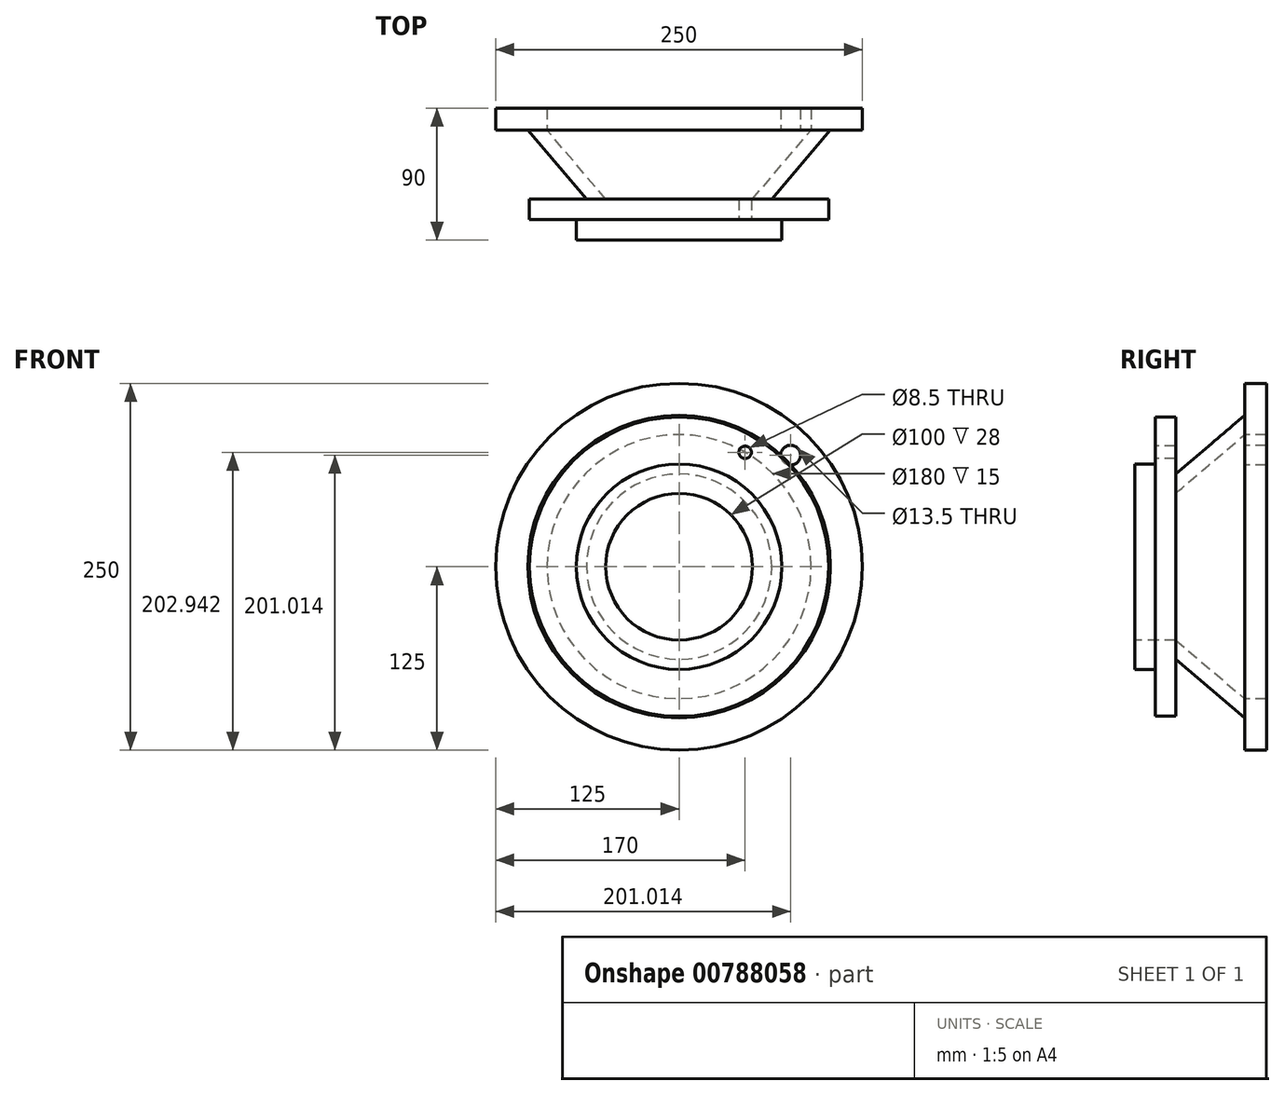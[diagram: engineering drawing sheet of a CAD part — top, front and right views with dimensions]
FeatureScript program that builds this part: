
annotation { "Feature Type Name" : "Feature", "Feature Type Description" : "" }
export const myFeature = defineFeature(function(context is Context, id is Id, definition is map)
    precondition{}
    {
        {
            var Q0;
            Q0=qCreatedBy(makeId("Front.planeOp"),FACE);
            var sketch = newSketch(context, id + "F0", { "sketchPlane" : qUnion([Q0])});
            skCircle(sketch, "E0", {"center": v(0, 0) * mm, "radius": 125 * mm});
            skSolve(sketch);
        }
        {
            var Q0;
            Q0=makeQuery(id+"F0.imprint","IMPRINT",FACE,{"disambiguationData":[TD([[makeQuery(id+"F0.imprint","IMPRINT",EDGE,{"derivedFrom":sQuery(id+"F0.wireOp",EDGE,"E0")}),1.0]])]});
            extrude(context, id + "F1", {"entities" : qUnion([Q0]), "depth" : 15 * mm, "offsetDistance" : 25 * mm});
        }
        {
            var Q0;
            Q0=makeQuery(id+"F1.opExtrude","CAP_FACE",FACE,{"disambiguationData":[OSD([sQuery(id+"F0.wireOp",EDGE,"E0")])],"isStart":false});
            var sketch = newSketch(context, id + "F2", { "sketchPlane" : qUnion([Q0])});
            skCircle(sketch, "E1", {"center": v(0, 0) * mm, "radius": 90 * mm});
            skSolve(sketch);
        }
        {
            var Q0;
            Q0=makeQuery(id+"F2.imprint","IMPRINT",FACE,{"disambiguationData":[TD([[makeQuery(id+"F2.imprint","IMPRINT",EDGE,{"derivedFrom":sQuery(id+"F2.wireOp",EDGE,"E1")}),-1.0]])]});
            cPlane(context, id + "F3", {"entities" : qUnion([Q0]), "cplaneType" : CPlaneType.OFFSET, "offset" : 47 * mm, "width" : 150 * mm, "height" : 150 * mm});
        }
        {
            var Q0;
            Q0=qCreatedBy(id+"F3.planeOp",FACE);
            var sketch = newSketch(context, id + "F4", { "sketchPlane" : qUnion([Q0])});
            skCircle(sketch, "E2", {"center": v(0, 0) * mm, "radius": 102 * mm});
            skSolve(sketch);
        }
        {
            var Q0;
            Q0=makeQuery(id+"F4.imprint","IMPRINT",FACE,{"disambiguationData":[TD([[makeQuery(id+"F4.imprint","IMPRINT",EDGE,{"derivedFrom":sQuery(id+"F4.wireOp",EDGE,"E2")}),1.0]])]});
            extrude(context, id + "F5", {"entities" : qUnion([Q0]), "depth" : 14 * mm, "offsetDistance" : 25 * mm});
        }
        {
            var Q0;
            Q0=makeQuery(id+"F5.opExtrude","CAP_FACE",FACE,{"disambiguationData":[OSD([sQuery(id+"F4.wireOp",EDGE,"E2")])],"isStart":false});
            var sketch = newSketch(context, id + "F6", { "sketchPlane" : qUnion([Q0])});
            skCircle(sketch, "E3", {"center": v(0, 0) * mm, "radius": 70 * mm});
            skSolve(sketch);
        }
        {
            var Q0;
            Q0=makeQuery(id+"F6.imprint","IMPRINT",FACE,{"disambiguationData":[TD([[makeQuery(id+"F6.imprint","IMPRINT",EDGE,{"derivedFrom":sQuery(id+"F6.wireOp",EDGE,"E3")}),1.0]])]});
            extrude(context, id + "F7", {"entities" : qUnion([Q0]), "operationType" : NewBodyOperationType.ADD, "depth" : 14 * mm, "offsetDistance" : 25 * mm});
        }
        {
            var Q0;
            Q0=makeQuery(id+"F5.opExtrude","CAP_FACE",FACE,{"disambiguationData":[OSD([sQuery(id+"F4.wireOp",EDGE,"E2")])],"isStart":false});
            var sketch = newSketch(context, id + "F8", { "sketchPlane" : qUnion([Q0])});
            skCircle(sketch, "E4", {"center": v(0, 0) * mm, "radius": 90 * mm, "construction": true});
            skLineSegment(sketch, "E5", {"start": v(0, 0) * mm, "end": v(0, 90) * mm, "construction": true});
            skLineSegment(sketch, "E6", {"start": v(0, 0) * mm, "end": v(45, 77.94) * mm, "construction": true});
            skSolve(sketch);
        }
        {
            var Q0;
            Q0=sQuery(id+"F8.wireOp",VERTEX,"E6.end");
            var Q1;
            Q1=makeQuery(id+"F5.opExtrude","SWEPT_BODY",BODY,{"disambiguationData":[OSD([sQuery(id+"F4.wireOp",EDGE,"E2")])]});
            var Q2;
            Q2=makeQuery(id+"F1.opExtrude","SWEPT_BODY",BODY,{"disambiguationData":[OSD([sQuery(id+"F0.wireOp",EDGE,"E0")])]});
            hole(context, id + "F9", {"style" : HoleStyle.SIMPLE, "endStyle" : HoleEndStyle.BLIND, "standardTappedOrClearance" : lookupTablePath({ "standard" : "ISO", "engagement" : "75%", "pitch" : "1.5 mm", "size" : "M10", "type" : "Tapped" }), "standardBlindInLast" : lookupTablePath({ "standard" : "ISO", "engagement" : "75%", "pitch" : "1.5 mm", "size" : "M10", "type" : "Tapped" }), "holeDiameter" : 8.5 * mm, "majorDiameter" : 10 * mm, "showTappedDepth" : true, "holeDepth" : 19.5 * mm, "isTappedThrough" : true, "tappedDepth" : 15 * mm, "tapClearance" : 3, "locations" : qUnion([Q0]), "scope" : qUnion([Q1, Q2])});
        }
        {
            var Q0;
            Q0=makeQuery(id+"F2.imprint","IMPRINT",FACE,{"disambiguationData":[TD([[makeQuery(id+"F2.imprint","IMPRINT",EDGE,{"derivedFrom":sQuery(id+"F2.wireOp",EDGE,"E1")}),1.0]])]});
            extrude(context, id + "F10", {"entities" : qUnion([Q0]), "operationType" : NewBodyOperationType.REMOVE, "oppositeDirection" : true, "depth" : 25 * mm, "offsetDistance" : 25 * mm});
        }
        {
            var Q0;
            Q0=makeQuery(id+"F1.opExtrude","CAP_FACE",FACE,{"disambiguationData":[OSD([sQuery(id+"F0.wireOp",EDGE,"E0")])],"isStart":false});
            var sketch = newSketch(context, id + "F11", { "sketchPlane" : qUnion([Q0])});
            skCircle(sketch, "E7", {"center": v(0, 0) * mm, "radius": 107.5 * mm, "construction": true});
            skLineSegment(sketch, "E8", {"start": v(0, 0) * mm, "end": v(0, 107.5) * mm, "construction": true});
            skLineSegment(sketch, "E9", {"start": v(0, 0) * mm, "end": v(76.01, 76.01) * mm, "construction": true});
            skSolve(sketch);
        }
        {
            var Q0;
            Q0=sQuery(id+"F11.wireOp",VERTEX,"E9.end");
            var Q1;
            Q1=makeQuery(id+"F1.opExtrude","SWEPT_BODY",BODY,{"disambiguationData":[OSD([sQuery(id+"F0.wireOp",EDGE,"E0")])]});
            hole(context, id + "F12", {"style" : HoleStyle.SIMPLE, "endStyle" : HoleEndStyle.BLIND, "holeDiameter" : 13.5 * mm, "majorDiameter" : 10 * mm, "holeDepth" : 20 * mm, "isTappedThrough" : true, "tappedDepth" : 15 * mm, "tapClearance" : 3, "locations" : qUnion([Q0]), "scope" : qUnion([Q1])});
        }
        {
            var Q0;
            Q0=makeQuery(id+"F7.opExtrude","CAP_FACE",FACE,{"disambiguationData":[OSD([sQuery(id+"F6.wireOp",EDGE,"E3")])],"isStart":false});
            var sketch = newSketch(context, id + "F13", { "sketchPlane" : qUnion([Q0])});
            skCircle(sketch, "E10", {"center": v(0, 0) * mm, "radius": 50 * mm});
            skSolve(sketch);
        }
        {
            var Q0;
            Q0=makeQuery(id+"F13.imprint","IMPRINT",FACE,{"disambiguationData":[TD([[makeQuery(id+"F13.imprint","IMPRINT",EDGE,{"derivedFrom":sQuery(id+"F13.wireOp",EDGE,"E10")}),1.0]])]});
            extrude(context, id + "F14", {"entities" : qUnion([Q0]), "operationType" : NewBodyOperationType.REMOVE, "endBound" : BoundingType.THROUGH_ALL, "oppositeDirection" : true, "depth" : 25 * mm, "offsetDistance" : 25 * mm});
        }
        {
            var Q0;
            Q0=qCreatedBy(makeId("Right.planeOp"),FACE);
            var sketch = newSketch(context, id + "F15", { "sketchPlane" : qUnion([Q0])});
            skLineSegment(sketch, "E11.0", {"start": v(-62, -102) * mm, "end": v(-62, 102) * mm});
            skLineSegment(sketch, "E12.0", {"start": v(-15, -125) * mm, "end": v(-15, 125) * mm});
            skLineSegment(sketch, "E13", {"start": v(-62, 50) * mm, "end": v(-15, 90) * mm});
            skLineSegment(sketch, "E14.0", {"start": v(-62, 63.13) * mm, "end": v(-15, 103.13) * mm});
            skSolve(sketch);
        }
        {
            var Q0;
            {var subQ0=sQuery(id+"F15.wireOp",EDGE,"E13");Q0=makeQuery(id+"F15.imprint","IMPRINT",FACE,{"disambiguationData":[TD([[makeQuery(id+"F15.imprint","IMPRINT",EDGE,{"derivedFrom":subQ0}),1.0]])]});}
            var Q1;
            Q1=makeQuery(id+"F5.opExtrude","CAP_EDGE",EDGE,{"disambiguationData":[OSD([sQuery(id+"F4.wireOp",EDGE,"E2")])],"isStart":false});
            revolve(context, id + "F16", {"surfaceOperationType" : NewSurfaceOperationType.NEW, "entities" : qUnion([Q0]), "axis" : qUnion([Q1]), "revolveType" : RevolveType.FULL});
        }
    });
